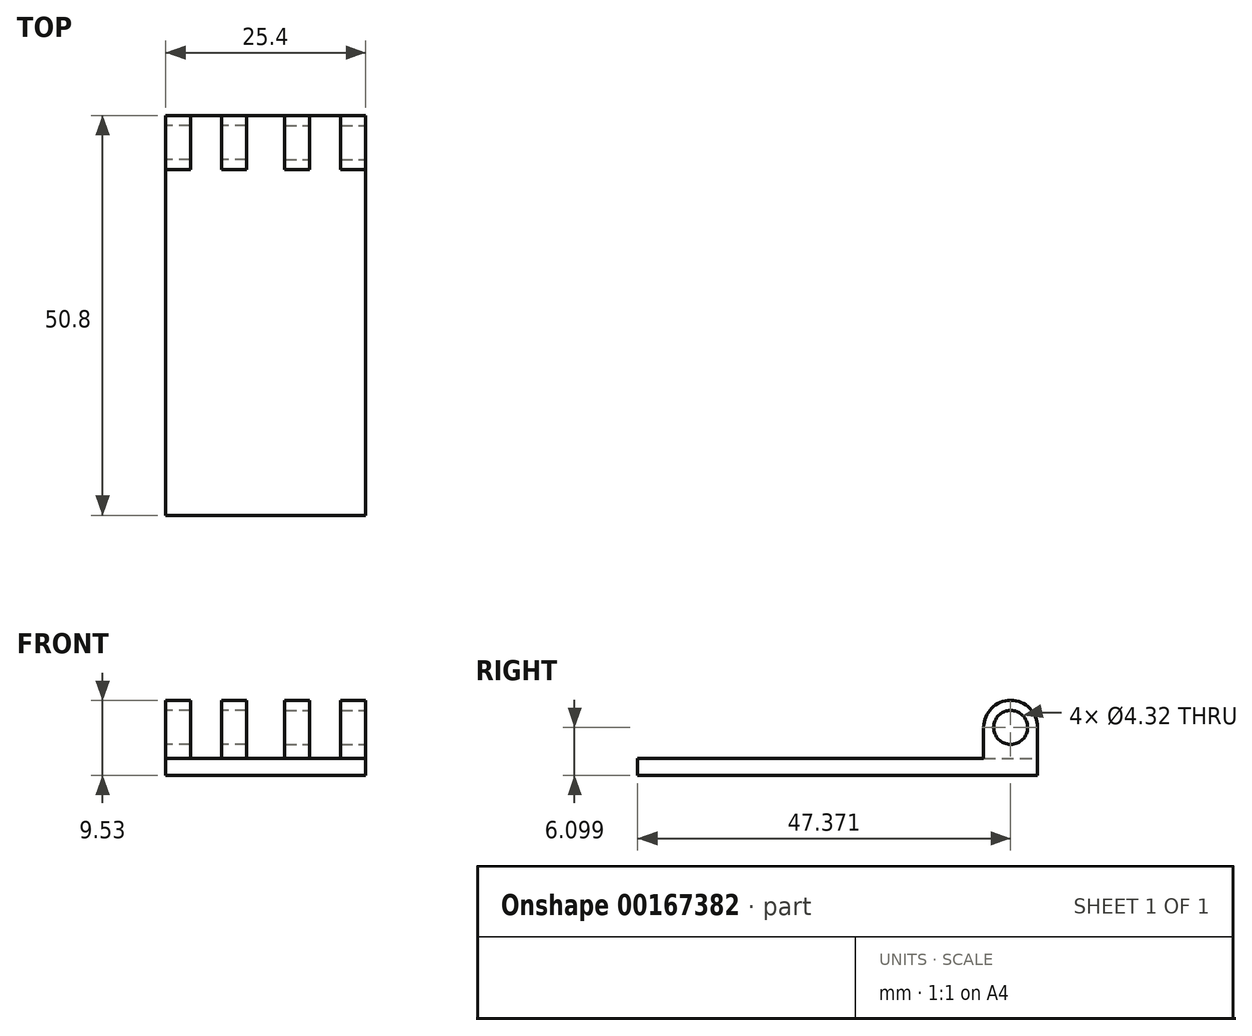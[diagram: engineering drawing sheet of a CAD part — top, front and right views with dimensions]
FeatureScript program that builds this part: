
annotation { "Feature Type Name" : "Feature", "Feature Type Description" : "" }
export const myFeature = defineFeature(function(context is Context, id is Id, definition is map)
    precondition{}
    {
        {
            var Q0;
            Q0=qCreatedBy(makeId("Right.planeOp"),FACE);
            var sketch = newSketch(context, id + "F0", { "sketchPlane" : qUnion([Q0])});
            skLineSegment(sketch, "E0.bottom", {"start": v(-39.26, 2.44) * mm, "end": v(11.54, 2.44) * mm});
            skLineSegment(sketch, "E0.top", {"start": v(-39.26, 4.6) * mm, "end": v(11.54, 4.6) * mm});
            skLineSegment(sketch, "E0.left", {"start": v(-39.26, 2.44) * mm, "end": v(-39.26, 4.6) * mm});
            skLineSegment(sketch, "E0.right", {"start": v(11.54, 2.44) * mm, "end": v(11.54, 4.6) * mm});
            skCircle(sketch, "E1", {"center": v(8.11, 8.54) * mm, "radius": 2.16 * mm});
            skCircle(sketch, "E2", {"center": v(8.11, 8.54) * mm, "radius": 3.43 * mm});
            skLineSegment(sketch, "E3", {"start": v(11.54, 2.44) * mm, "end": v(11.54, 8.54) * mm});
            skLineSegment(sketch, "E4", {"start": v(4.68, 8.54) * mm, "end": v(4.68, 2.44) * mm});
            skSolve(sketch);
        }
        {
            var Q0;
            {var subQ0=sQuery(id+"F0.wireOp",EDGE,"E0.left");Q0=makeQuery(id+"F0.imprint","IMPRINT",FACE,{"disambiguationData":[TD([[makeQuery(id+"F0.imprint","IMPRINT",EDGE,{"derivedFrom":subQ0}),-1.0]])]});}
            var Q1;
            {var subQ0=sQuery(id+"F0.wireOp",EDGE,"E3");var subQ1=sQuery(id+"F0.wireOp",EDGE,"E0.bottom");var subQ2=makeQuery(id+"F0.imprint","INTERSECT",VERTEX,{"derivedFrom":[subQ1,subQ0]});Q1=makeQuery(id+"F0.imprint","IMPRINT",FACE,{"disambiguationData":[TD([[makeQuery(id+"F0.imprint","IMPRINT",EDGE,{"disambiguationData":[TD([[subQ2,1.0]])],"derivedFrom":subQ1}),1.0]])]});}
            extrude(context, id + "F1", {"entities" : qUnion([Q0, Q1]), "depth" : 25.4 * mm});
        }
        {
            var Q0;
            {var subQ0=sQuery(id+"F0.wireOp",EDGE,"E3");var subQ1=sQuery(id+"F0.wireOp",EDGE,"E0.top");var subQ2=makeQuery(id+"F0.imprint","INTERSECT",VERTEX,{"derivedFrom":[subQ1,subQ0]});Q0=makeQuery(id+"F0.imprint","IMPRINT",FACE,{"disambiguationData":[TD([[makeQuery(id+"F0.imprint","IMPRINT",EDGE,{"disambiguationData":[TD([[subQ2,1.0]])],"derivedFrom":subQ1}),1.0]])]});}
            var Q1;
            {var subQ0=sQuery(id+"F0.wireOp",EDGE,"E4");var subQ1=sQuery(id+"F0.wireOp",EDGE,"E0.top");var subQ2=makeQuery(id+"F0.imprint","INTERSECT",VERTEX,{"derivedFrom":[subQ1,subQ0]});Q1=makeQuery(id+"F0.imprint","IMPRINT",FACE,{"disambiguationData":[TD([[makeQuery(id+"F0.imprint","IMPRINT",EDGE,{"disambiguationData":[TD([[subQ2,-1.0]])],"derivedFrom":subQ1}),1.0]])]});}
            var Q2;
            Q2=makeQuery(id+"F0.imprint","IMPRINT",FACE,{"disambiguationData":[TD([[makeQuery(id+"F0.imprint","IMPRINT",EDGE,{"derivedFrom":sQuery(id+"F0.wireOp",EDGE,"E1")}),-1.0]])]});
            extrude(context, id + "F2", {"entities" : qUnion([Q0, Q1, Q2]), "operationType" : NewBodyOperationType.ADD, "depth" : 3.17 * mm});
        }
        {
            var Q0;
            Q0=makeQuery(id+"F1.opExtrude","CAP_FACE",FACE,{"disambiguationData":[OSD([sQuery(id+"F0.wireOp",EDGE,"E0.bottom"),sQuery(id+"F0.wireOp",EDGE,"E0.top"),sQuery(id+"F0.wireOp",EDGE,"E0.left"),sQuery(id+"F0.wireOp",EDGE,"E3")])],"isStart":false});
            var sketch = newSketch(context, id + "F3", { "sketchPlane" : qUnion([Q0])});
            skCircle(sketch, "E5.0", {"center": v(8.11, 8.54) * mm, "radius": 3.43 * mm});
            skCircle(sketch, "E6.0", {"center": v(8.11, 8.54) * mm, "radius": 2.16 * mm});
            skLineSegment(sketch, "E7.0", {"start": v(4.68, 8.54) * mm, "end": v(4.68, 2.44) * mm});
            skLineSegment(sketch, "E8.0", {"start": v(-39.26, 4.6) * mm, "end": v(11.54, 4.6) * mm});
            skLineSegment(sketch, "E9.0", {"start": v(11.54, 2.44) * mm, "end": v(11.54, 8.54) * mm});
            skSolve(sketch);
        }
        {
            var Q0;
            Q0 = qSketchRegion(id + "F3", true);
            extrude(context, id + "F4", {"entities" : qUnion([Q0]), "operationType" : NewBodyOperationType.ADD, "oppositeDirection" : true, "depth" : 3.17 * mm});
        }
        {
            var Q0;
            Q0=qCreatedBy(makeId("Right.planeOp"),FACE);
            cPlane(context, id + "F5", {"entities" : qUnion([Q0]), "cplaneType" : CPlaneType.OFFSET, "offset" : 7.11 * mm, "width" : 152.4 * mm, "height" : 152.4 * mm});
        }
        {
            var Q0;
            Q0=qCreatedBy(id+"F5.planeOp",FACE);
            var sketch = newSketch(context, id + "F6", { "sketchPlane" : qUnion([Q0])});
            skCircle(sketch, "E10.0", {"center": v(8.11, 8.54) * mm, "radius": 2.16 * mm});
            skArc(sketch, "E10.1", {"start": v(11.54, 8.54) * mm, "mid": v(8.11, 11.97) * mm, "end": v(4.68, 8.54) * mm});
            skLineSegment(sketch, "E11.0", {"start": v(4.68, 4.6) * mm, "end": v(11.54, 4.6) * mm});
            skLineSegment(sketch, "E12.0", {"start": v(11.54, 4.6) * mm, "end": v(11.54, 8.54) * mm});
            skLineSegment(sketch, "E12.1", {"start": v(4.68, 8.54) * mm, "end": v(4.68, 4.6) * mm});
            skSolve(sketch);
        }
        {
            var Q0;
            Q0 = qSketchRegion(id + "F6", true);
            extrude(context, id + "F7", {"entities" : qUnion([Q0]), "operationType" : NewBodyOperationType.ADD, "depth" : 3.17 * mm});
        }
        {
            var Q0;
            Q0=makeQuery(id+"F4.boolean.opBoolean","MERGE",FACE,{"derivedFrom":[makeQuery(id+"F1.opExtrude","CAP_FACE",FACE,{"disambiguationData":[OSD([sQuery(id+"F0.wireOp",EDGE,"E0.bottom"),sQuery(id+"F0.wireOp",EDGE,"E0.top"),sQuery(id+"F0.wireOp",EDGE,"E0.left"),sQuery(id+"F0.wireOp",EDGE,"E3")])],"isStart":false}),makeQuery(id+"F4.opExtrude","CAP_FACE",FACE,{"disambiguationData":[OSD([sQuery(id+"F3.wireOp",EDGE,"E5.0"),sQuery(id+"F3.wireOp",EDGE,"E6.0"),sQuery(id+"F3.wireOp",EDGE,"E7.0"),sQuery(id+"F3.wireOp",EDGE,"E8.0"),sQuery(id+"F3.wireOp",EDGE,"E9.0")])],"isStart":true})]});
            cPlane(context, id + "F8", {"entities" : qUnion([Q0]), "cplaneType" : CPlaneType.OFFSET, "offset" : 7.11 * mm, "oppositeDirection" : true, "width" : 152.4 * mm, "height" : 152.4 * mm});
        }
        {
            var Q0;
            Q0=qCreatedBy(id+"F8.planeOp",FACE);
            var sketch = newSketch(context, id + "F9", { "sketchPlane" : qUnion([Q0])});
            skLineSegment(sketch, "E13.0", {"start": v(4.68, 4.6) * mm, "end": v(11.54, 4.6) * mm});
            skLineSegment(sketch, "E13.1", {"start": v(11.54, 4.6) * mm, "end": v(11.54, 8.54) * mm});
            skArc(sketch, "E13.2", {"start": v(11.54, 8.54) * mm, "mid": v(8.11, 11.97) * mm, "end": v(4.68, 8.54) * mm});
            skCircle(sketch, "E13.3", {"center": v(8.11, 8.54) * mm, "radius": 2.16 * mm});
            skLineSegment(sketch, "E13.4", {"start": v(4.68, 8.54) * mm, "end": v(4.68, 4.6) * mm});
            skPoint(sketch, "E13.5", {"position": v(8.11, 4.6) * mm});
            skSolve(sketch);
        }
        {
            var Q0;
            Q0 = qSketchRegion(id + "F9", true);
            extrude(context, id + "F10", {"entities" : qUnion([Q0]), "operationType" : NewBodyOperationType.ADD, "oppositeDirection" : true, "depth" : 3.17 * mm});
        }
    });
